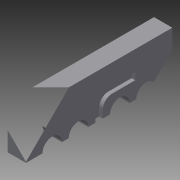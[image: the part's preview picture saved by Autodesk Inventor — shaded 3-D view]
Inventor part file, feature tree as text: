
AUTODESK INVENTOR PART (.ipt)
format: ipt  version: 2015 (Build 190159000, 159)  size: 114,688 bytes
history: native  units: in
note: dims shown in document units (in); Inventor stores cm internally (conversion verified against a paired STEP export)
features: extrude x2, sketch x2, projected_geometry x1
ambient origin geometry x8: Origin, YZ Plane, XZ Plane, XY Plane, X Axis, Y Axis, Z Axis, Center Point
bodies: Solid1 (feature_tree)
feature tree (5):
  extrude  "Extrusion1"  Depth=2.0in
  extrude  "Extrusion2"  Depth=0.1in
  sketch  "Sketch1"  dims[d0=0.6in d1=2.0in]
  sketch  "Sketch2"  dims[d2=0.25in d3=0.0in d4=0.1in d5=0.125in d6=0.05in d7=0.0in]
  projected_geometry  "Projected Loop1"
